# Revit family: Zumtobel LINARIA
name_source: partatom
category: Lighting Fixtures
revit_build: Autodesk Revit 2016 (Build: 20150220_1215(x64)
units: mm (PartAtom-declared; Revit-internal decimal feet)

## family parameters
Cut with Voids When Loaded = No
Host = Face
Light Source = Yes
OmniClass Number = 23.80.70.11
OmniClass Title = Luminaries for Internal Lighting
Part Type = Normal
Room Calculation Point = No
Round Connector Dimension = Use Diameter
Shared = No

## types (16) — shared parameters
Assembly Code = D5020200
Color Filter = 16777215
Cover = Zumtobel_PMMA_Self_llumination_Opaque
Dimming Lamp Color Temperature Shift = <None>
Emit Shape Visible in Rendering = Yes
Emit from Rectangle Length = 30 mm  [stored 0.0984252 ft]
Manufacturer = Zumtobel Lighting
Tilt Angle = 90.00°
URL = http://www.zumtobel.com
Voltage = 230 V
Width = 30 mm  [stored 0.0984252 ft]
zero-valued in all types: Default Elevation

## per-type parameters (varying)
| type | Apparent Load | Body | Description | Emit from Rectangle Width | Height | Lamp | Length | Model | Photometric Web File |
| LINARIA 2x1/28W T16-D Electronic | 61 VA | Zumtobel_Metal_White | Seamless batten luminaire | 2372 mm  [stored 7.78215 ft] | 61 mm  [stored 0.200131 ft] | T16-D | 2372 mm  [stored 7.78215 ft] | 42181141+22162106 | D27459V3.IES |
| LINARIA 2x1/28W T16-D Dimmable | 61 VA | Zumtobel_Metal_White | Seamless batten luminaire | 2372 mm  [stored 7.78215 ft] | 61 mm  [stored 0.200131 ft] | T16-D | 2372 mm  [stored 7.78215 ft] | 42924547+22162106 | D27459V3.IES |
| LINARIA 2x1/54W T16-D Electronic | 115 VA | Zumtobel_Metal_White | Seamless batten luminaire | 2372 mm  [stored 7.78215 ft] | 61 mm  [stored 0.200131 ft] | T16-D | 2372 mm  [stored 7.78215 ft] | 42177516+22162106 | D27459V8.IES |
| LINARIA 2x1/54W T16-D Dimmable | 118 VA | Zumtobel_Metal_White | Seamless batten luminaire | 2372 mm  [stored 7.78215 ft] | 61 mm  [stored 0.200131 ft] | T16-D | 2372 mm  [stored 7.78215 ft] | 42177517+22162106 | D27459V8.IES |
| LINARIA 1x1/28W T16-D Electronic | 32 VA | Zumtobel_Metal_White | Seamless batten luminaire | 1188 mm  [stored 3.89764 ft] | 61 mm  [stored 0.200131 ft] | T16-D | 1188 mm  [stored 3.89764 ft] | 42181138+22162106 | D27459U3.IES |
| LINARIA 1x1/28W T16-D Dimmable | 32 VA | Zumtobel_Metal_White | Seamless batten luminaire | 1188 mm  [stored 3.89764 ft] | 61 mm  [stored 0.200131 ft] | T16-D | 1188 mm  [stored 3.89764 ft] | 42924565+22162106 | D27459U3.IES |
| LINARIA 1x1/54W T16-D Electronic | 58 VA | Zumtobel_Metal_White | Seamless batten luminaire | 1188 mm  [stored 3.89764 ft] | 61 mm  [stored 0.200131 ft] | T16-D | 1188 mm  [stored 3.89764 ft] | 42177510+22162106 | D27459U8.IES |
| LINARIA 1x1/54W T16-D Dimmable | 60 VA | Zumtobel_Metal_White | Seamless batten luminaire | 1188 mm  [stored 3.89764 ft] | 61 mm  [stored 0.200131 ft] | T16-D | 1188 mm  [stored 3.89764 ft] | 42177511+22162106 | D27459U8.IES |
| LINARIA LED L765 Dimmable | 21 VA | Zumtobel_Metal_White | Single batten LED luminaire | 765 mm  [stored 2.50984 ft] | 67 mm | LED | 765 mm  [stored 2.50984 ft] | 42182357+22162106 | D33994AA_LINARIA_21W_840_L760.IES |
| LINARIA LED L1015 Dimmable | 28 VA | Zumtobel_Metal_White | Single batten LED luminaire | 1015 mm  [stored 3.33005 ft] | 67 mm | LED | 1015 mm  [stored 3.33005 ft] | 42182358+22162106 | D33994AA_LINARIA_28W_840_L1010.IES |
| LINARIA LED L2015 Dimmable | 56 VA | Zumtobel_Metal_White | Single batten LED luminaire | 2015 mm  [stored 6.61089 ft] | 67 mm | LED | 2015 mm  [stored 6.61089 ft] | 42182359+22162106 | D33994AA_LINARIA_57W_840_L2010.IES |
| LINARIA LED L608 | 15 VA | Zumtobel_Metal_Aluminium | Single batten LED luminaire | 608 mm  [stored 1.99475 ft] | 67 mm | LED | 608 mm  [stored 1.99475 ft] | 42184110 | 42184110_(STD_LEO).IES |
| LINARIA LED L908 | 22 VA | Zumtobel_Metal_Aluminium | Single batten LED luminaire | 908 mm  [stored 2.979 ft] | 67 mm | LED | 908 mm  [stored 2.979 ft] | 42184111 | 42184111_(STD_LEO).IES |
| LINARIA LED L1208 | 31 VA | Zumtobel_Metal_Aluminium | Single batten LED luminaire | 1208 mm  [stored 3.96325 ft] | 67 mm | LED | 1208 mm  [stored 3.96325 ft] | 42184112 | 42184112_(STD_LEO).IES |
| LINARIA LED L1508 | 39 VA | Zumtobel_Metal_Aluminium | Single batten LED luminaire | 1508 mm  [stored 4.94751 ft] | 67 mm | LED | 1508 mm  [stored 4.94751 ft] | 42184113 | 42184113_(STD_LEO).IES |
| LINARIA LED L1808 | 44 VA | Zumtobel_Metal_Aluminium | Single batten LED luminaire | 1808 mm  [stored 5.93176 ft] | 67 mm | LED | 1808 mm  [stored 5.93176 ft] | 42184114 | 42184114_(STD_LEO).IES |

note: [stored X ft] marks values corroborated as IEEE doubles in the binary element streams (Revit-internal decimal feet)

## geometry (parser evidence)
native form markers: Blend x33, Sweep x1
no freeform markers — native parametric forms only
